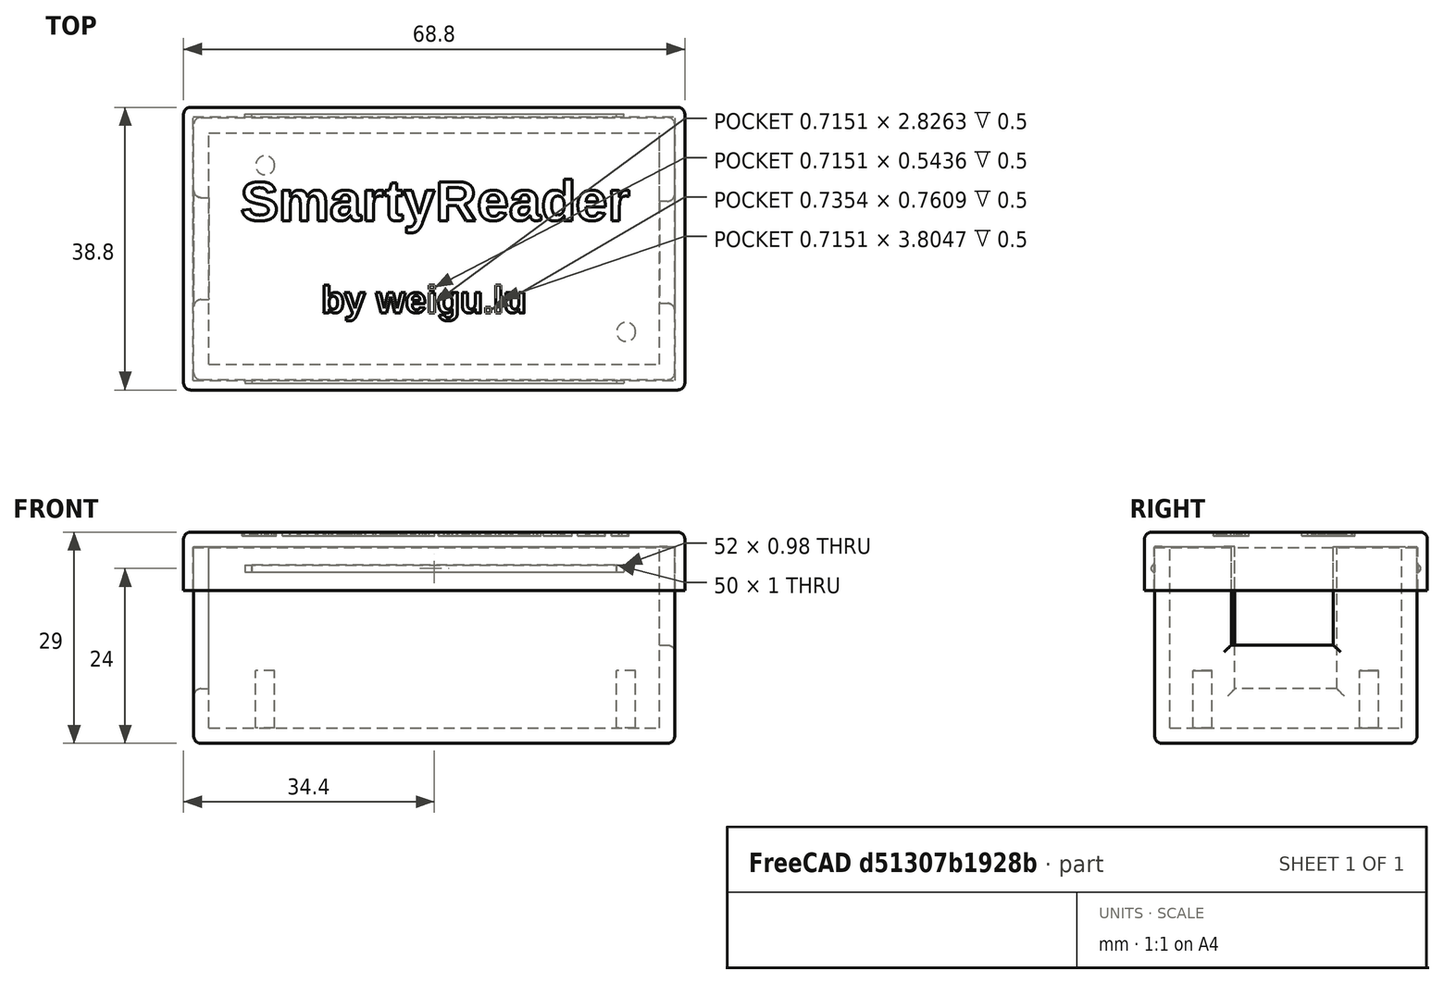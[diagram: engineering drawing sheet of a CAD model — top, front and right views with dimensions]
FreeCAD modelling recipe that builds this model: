
FCSTD DOCUMENT  (FreeCAD 0.20R29410 (Git))
Label: SmartyReader_P1_WiFi
License: All rights reserved
LicenseURL: http://en.wikipedia.org/wiki/All_rights_reserved
objects: Part::Cut×8, Part::Box×6, Part::Cylinder×6, Part::MultiFuse×2, Part::Part2DObjectPython×2, Part::Extrusion×2, Part::Fillet×2
note: 28 computed .brp shape members not serialized (recipe doc carries the construction recipe); baked Part::Feature solids carry a one-line shape summary decoded from their .brp

FEATURE [Part::Box] Box  label="Cube"
  AttacherType = Attacher::AttachEngine3D
  Height = 27
  Length = 66
  Width = 36
FEATURE [Part::Box] Box001  label="Cube001"
  AttacherType = Attacher::AttachEngine3D
  Height = 24.9
  Length = 61.8
  Placement = pos=(2.1,2.1,2.1) rot=(0,0,1;0rad)
  Width = 31.8
FEATURE [Part::Cut] Cut
  Base = -> Box
  Tool = -> Box001
FEATURE [Part::Box] Box002  label="Cube002"
  AttacherType = Attacher::AttachEngine3D
  Height = 19.5
  Length = 4
  Placement = pos=(-1,11,7.5) rot=(0,0,1;0rad)
  Width = 14
FEATURE [Part::Cut] Cut001
  Base = -> Cut
  Tool = -> Box002
FEATURE [Part::Cylinder] Cylinder
  Angle = 360
  AttacherType = Attacher::AttachEngine3D
  FirstAngle = 0
  Height = 8
  Placement = pos=(9.81,29.43,2) rot=(0,0,1;0rad)
  Radius = 1.3
  SecondAngle = 0
FEATURE [Part::Cylinder] Cylinder001
  Angle = 360
  AttacherType = Attacher::AttachEngine3D
  FirstAngle = 0
  Height = 8
  Placement = pos=(59.34,6.57,2) rot=(0,0,1;0rad)
  Radius = 1.3
  SecondAngle = 0
FEATURE [Part::Box] Box003  label="Cube003"
  AttacherType = Attacher::AttachEngine3D
  Height = 14
  Length = 4
  Placement = pos=(63,10.5,13.5) rot=(0,0,1;0rad)
  Width = 14
FEATURE [Part::Cut] Cut002
  Base = -> Cut001
  Tool = -> Box003
FEATURE [Part::MultiFuse] Fusion
  Shapes = -> [Cut002,Cylinder,Cylinder001]
FEATURE [Part::Box] Box004  label="Cube004"
  AttacherType = Attacher::AttachEngine3D
  Height = 8
  Length = 68.8
  Placement = pos=(-1.4,-1.4,21) rot=(0,0,1;0rad)
  Width = 38.8
FEATURE [Part::Box] Box005  label="Cube005"
  AttacherType = Attacher::AttachEngine3D
  Height = 5.9
  Length = 66.2
  Placement = pos=(-0.1,-0.1,21) rot=(0,0,1;0rad)
  Width = 36.2
FEATURE [Part::Cut] Cut003
  Base = -> Box004
  Tool = -> Box005
FEATURE [Part::Part2DObjectPython] ShapeString  # Draft 2D object (typed FeaturePython)
  FontFile = /savit/freecad/fonts/truetype/liberation/LiberationSans-Bold.ttf
  Placement = pos=(6.42,21.79,36) rot=(0,0,1;0rad)
  Size = 6
  String = SmartyReader
  Tracking = 0
FEATURE [Part::Part2DObjectPython] ShapeString001  # Draft 2D object (typed FeaturePython)
  FontFile = /savit/freecad/fonts/truetype/liberation/LiberationSans-Bold.ttf
  Placement = pos=(17.5,9.16,35) rot=(0,0,1;0rad)
  Size = 4
  String = by weigu.lu
  Tracking = 0
FEATURE [Part::Extrusion] Extrude
  Base = -> ShapeString
  Dir = (0,0,1)
  DirMode = 2
  FaceMakerClass = Part::FaceMakerBullseye
  LengthFwd = 2
  LengthRev = 0
  Placement = pos=(0,0,-7.5) rot=(0,0,1;0rad)
  Solid = false
  Symmetric = false
FEATURE [Part::Extrusion] Extrude001
  Base = -> ShapeString001
  Dir = (0,0,1)
  DirMode = 2
  FaceMakerClass = Part::FaceMakerBullseye
  LengthFwd = 2
  LengthRev = 0
  Placement = pos=(0,0,-6.5) rot=(0,0,1;0rad)
  Solid = false
  Symmetric = false
FEATURE [Part::Cut] Cut004
  Base = -> Cut003
  Tool = -> Extrude
FEATURE [Part::Cut] Cut005  label="Lid001"
  Base = -> Cut004
  Tool = -> Extrude001
FEATURE [Part::Fillet] Fillet001  label="Lid002"
  Base = -> Cut005
  Edges = 8 edges r=1: [Edge1,Edge2,Edge3,Edge6,Edge7,Edge8,Edge9,Edge572]
FEATURE [Part::Cylinder] Cylinder002
  Angle = 360
  AttacherType = Attacher::AttachEngine3D
  FirstAngle = 0
  Height = 50
  Placement = pos=(8,0,24) rot=(0,1,0;1.5708rad)
  Radius = 0.5
  SecondAngle = 0
FEATURE [Part::Cylinder] Cylinder003
  Angle = 360
  AttacherType = Attacher::AttachEngine3D
  FirstAngle = 0
  Height = 50
  Placement = pos=(8,36,24) rot=(0,1,0;1.5708rad)
  Radius = 0.5
  SecondAngle = 0
FEATURE [Part::Cylinder] Cylinder004
  Angle = 360
  AttacherType = Attacher::AttachEngine3D
  FirstAngle = 0
  Height = 52
  Placement = pos=(7,36,24) rot=(0,1,0;1.5708rad)
  Radius = 0.5
  SecondAngle = 0
FEATURE [Part::Cylinder] Cylinder005
  Angle = 360
  AttacherType = Attacher::AttachEngine3D
  FirstAngle = 0
  Height = 52
  Placement = pos=(7,0,24) rot=(0,1,0;1.5708rad)
  Radius = 0.5
  SecondAngle = 0
FEATURE [Part::Cut] Cut006
  Base = -> Fillet001
  Tool = -> Cylinder004
FEATURE [Part::Cut] Cut007  label="Lid"
  Base = -> Cut006
  Tool = -> Cylinder005
FEATURE [Part::Fillet] Fillet
  Base = -> Fusion
  Edges = 14 edges r=1: [Edge33,Edge35,Edge37,Edge43,Edge45,Edge46,Edge47,Edge48,Edge49,Edge50,Edge51,Edge52,Edge53,Edge54]
FEATURE [Part::MultiFuse] Fusion001  label="Case"
  Shapes = -> [Fillet,Cylinder003,Cylinder002]
